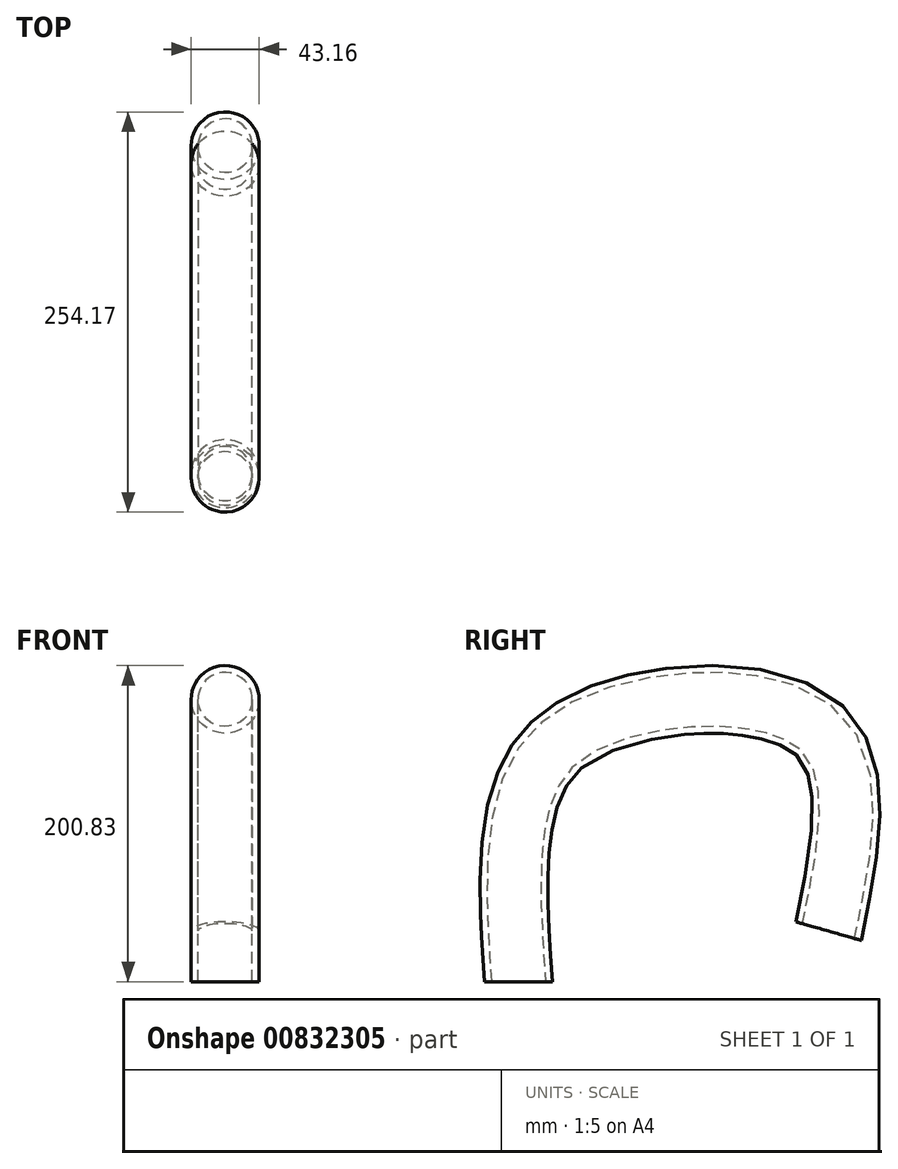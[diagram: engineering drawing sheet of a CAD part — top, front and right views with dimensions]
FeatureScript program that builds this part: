
annotation { "Feature Type Name" : "Feature", "Feature Type Description" : "" }
export const myFeature = defineFeature(function(context is Context, id is Id, definition is map)
    precondition{}
    {
        {
            var Q0;
            Q0=qCreatedBy(makeId("Right.planeOp"),FACE);
            var sketch = newSketch(context, id + "F0", { "sketchPlane" : qUnion([Q0])});
            skFitSpline(sketch, "E0", {"points": [v(0, 0) * mm, v(0, 100.29) * mm, v(43.16, 163.02) * mm, v(189.72, 160.85) * mm, v(196.91, 32.16) * mm], "startDerivative": vector(-31.6, 444.15) * mm, "endDerivative": vector(-120.79, -579.33) * mm});
            skSolve(sketch);
        }
        {
            var Q0;
            Q0=qCreatedBy(makeId("Top.planeOp"),FACE);
            var sketch = newSketch(context, id + "F1", { "sketchPlane" : qUnion([Q0])});
            skCircle(sketch, "E1", {"center": v(0, 0) * mm, "radius": 21.58 * mm});
            skCircle(sketch, "E2", {"center": v(0, 0) * mm, "radius": 17.2 * mm});
            skSolve(sketch);
        }
        {
            var Q0;
            Q0=makeQuery(id+"F1.imprint","IMPRINT",FACE,{"disambiguationData":[TD([[makeQuery(id+"F1.imprint","IMPRINT",EDGE,{"derivedFrom":sQuery(id+"F1.wireOp",EDGE,"E1")}),1.0]])]});
            var Q1;
            Q1=sQuery(id+"F0.wireOp",EDGE,"E0");
            sweep(context, id + "F2", {"profiles" : qUnion([Q0]), "path" : qUnion([Q1])});
        }
    });
